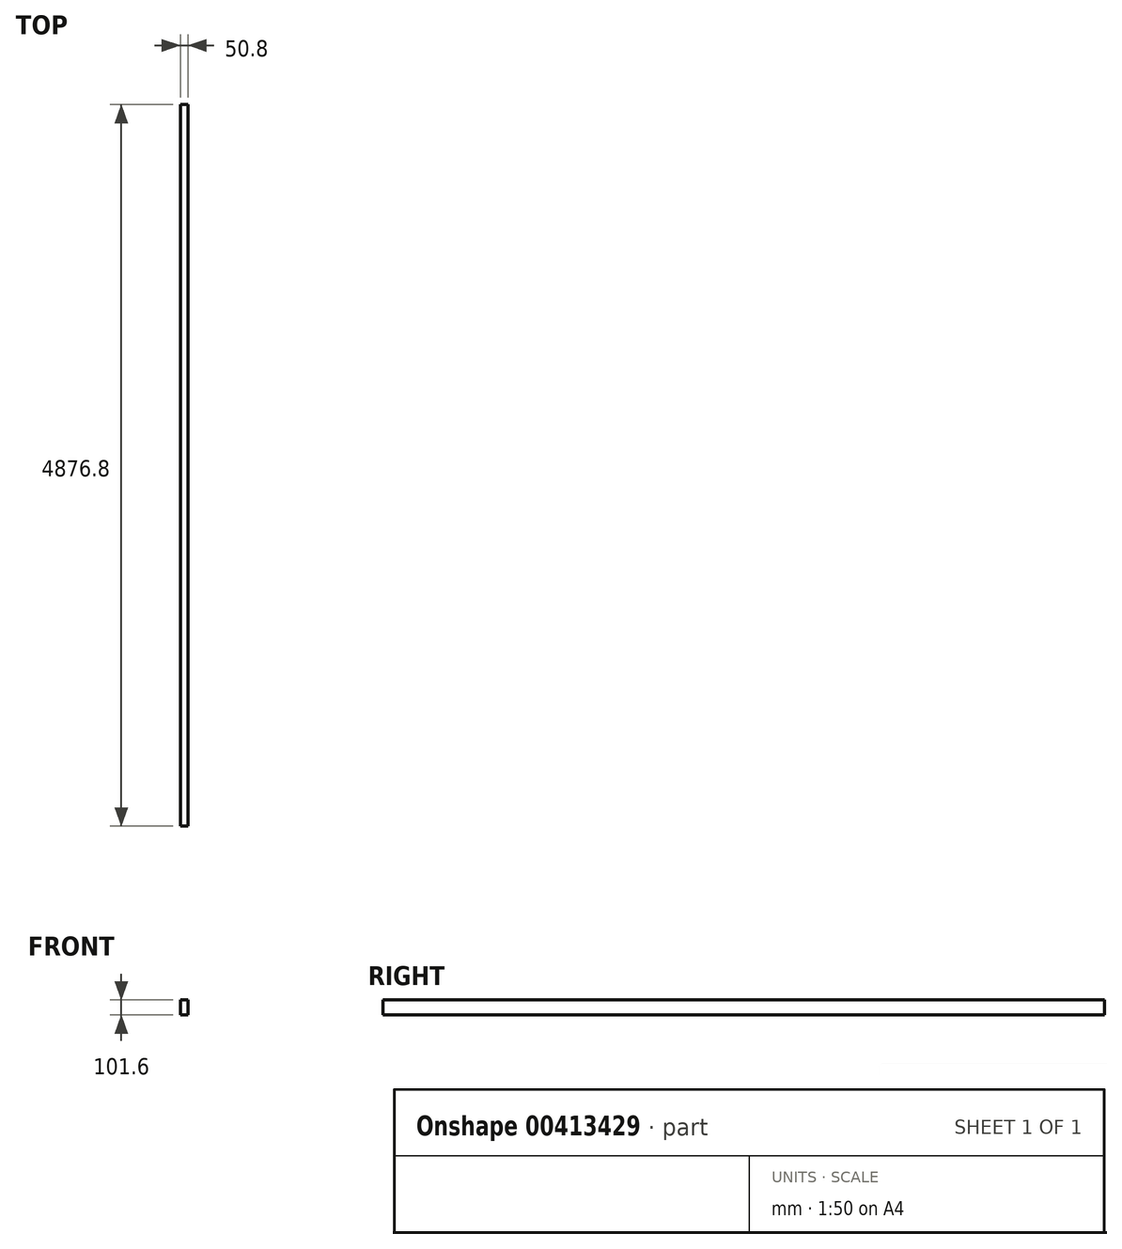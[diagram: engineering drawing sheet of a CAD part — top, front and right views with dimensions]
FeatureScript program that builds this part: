
annotation { "Feature Type Name" : "Feature", "Feature Type Description" : "" }
export const myFeature = defineFeature(function(context is Context, id is Id, definition is map)
    precondition{}
    {
        {
            var Q0;
            Q0=qCreatedBy(makeId("Front.planeOp"),FACE);
            var sketch = newSketch(context, id + "F0", { "sketchPlane" : qUnion([Q0])});
            skLineSegment(sketch, "E0.bottom", {"start": v(25.4, -50.8) * mm, "end": v(-25.4, -50.8) * mm});
            skLineSegment(sketch, "E0.top", {"start": v(25.4, 50.8) * mm, "end": v(-25.4, 50.8) * mm});
            skLineSegment(sketch, "E0.left", {"start": v(25.4, -50.8) * mm, "end": v(25.4, 50.8) * mm});
            skLineSegment(sketch, "E0.right", {"start": v(-25.4, -50.8) * mm, "end": v(-25.4, 50.8) * mm});
            skPoint(sketch, "E0.middle", {"position": v(0, 0) * mm});
            skSolve(sketch);
        }
        {
            var Q0;
            Q0=makeQuery(id+"F0.imprint","IMPRINT",FACE,{"disambiguationData":[TD([[makeQuery(id+"F0.imprint","IMPRINT",EDGE,{"derivedFrom":sQuery(id+"F0.wireOp",EDGE,"E0.bottom")}),-1.0]])]});
            extrude(context, id + "F1", {"entities" : qUnion([Q0]), "depth" : 4876.8 * mm});
        }
    });
